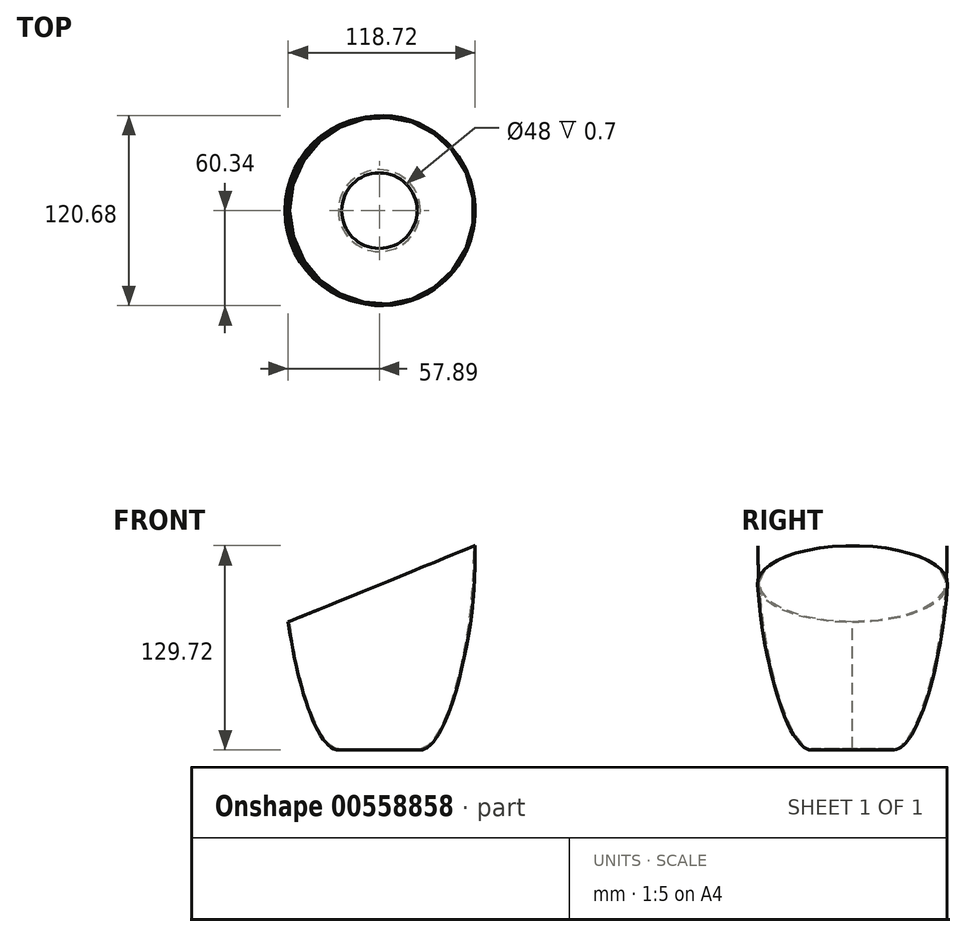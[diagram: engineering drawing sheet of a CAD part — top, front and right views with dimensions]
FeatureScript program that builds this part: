
annotation { "Feature Type Name" : "Feature", "Feature Type Description" : "" }
export const myFeature = defineFeature(function(context is Context, id is Id, definition is map)
    precondition{}
    {
        {
            var Q0;
            Q0=qCreatedBy(makeId("Front.planeOp"),FACE);
            var sketch = newSketch(context, id + "F0", { "sketchPlane" : qUnion([Q0])});
            skLineSegment(sketch, "E0", {"start": v(0, 0) * mm, "end": v(0, 79.4) * mm, "construction": true});
            skLineSegment(sketch, "E1", {"start": v(-24, 0) * mm, "end": v(-24, 0.7) * mm});
            skLineSegment(sketch, "E2", {"start": v(-26, 0) * mm, "end": v(-24, 0) * mm});
            skFitSpline(sketch, "E3", {"points": [v(-26, 0.7) * mm, v(-60, 130) * mm], "startDerivative": vector(-49.34, 0.23) * mm, "endDerivative": vector(3.08, 176.72) * mm});
            skLineSegment(sketch, "E4", {"start": v(-57.02, 130) * mm, "end": v(57.16, 130) * mm, "construction": true});
            skFitSpline(sketch, "E5.0", {"points": [v(-26, 0) * mm, v(-26.58, 0) * mm, v(-27.73, 0.16) * mm, v(-29.43, 0.83) * mm, v(-31.1, 1.89) * mm, v(-32.72, 3.3) * mm, v(-34.33, 5.07) * mm, v(-36.44, 7.86) * mm, v(-39.03, 12.13) * mm, v(-42.04, 18.4) * mm, v(-44.94, 25.72) * mm, v(-47.69, 33.96) * mm, v(-50.26, 43) * mm, v(-52.63, 52.72) * mm, v(-55.47, 66.45) * mm, v(-58.35, 84.73) * mm, v(-60.47, 107.51) * mm, v(-60.83, 122.63) * mm, v(-60.7, 130.01) * mm]});
            skLineSegment(sketch, "E6", {"start": v(-26, 0) * mm, "end": v(-26, 0) * mm});
            skLineSegment(sketch, "E7", {"start": v(-60.7, 130.01) * mm, "end": v(-60, 130) * mm});
            skLineSegment(sketch, "E8", {"start": v(-26, 0.7) * mm, "end": v(-24, 0.7) * mm});
            skSolve(sketch);
        }
        {
            var Q0;
            Q0=makeQuery(id+"F0.imprint","IMPRINT",FACE,{"disambiguationData":[TD([[makeQuery(id+"F0.imprint","IMPRINT",EDGE,{"derivedFrom":sQuery(id+"F0.wireOp",EDGE,"E1")}),1.0]])]});
            var Q1;
            Q1=sQuery(id+"F0.wireOp",EDGE,"E0");
            revolve(context, id + "F1", {"surfaceOperationType" : NewSurfaceOperationType.NEW, "entities" : qUnion([Q0]), "axis" : qUnion([Q1]), "revolveType" : RevolveType.FULL});
        }
        {
            var Q0;
            Q0=qCreatedBy(makeId("Front.planeOp"),FACE);
            var sketch = newSketch(context, id + "F2", { "sketchPlane" : qUnion([Q0])});
            skLineSegment(sketch, "E9", {"start": v(66.83, 132.22) * mm, "end": v(-75.49, 74.11) * mm});
            skLineSegment(sketch, "E10", {"start": v(-75.49, 74.11) * mm, "end": v(-75.49, 154.84) * mm});
            skLineSegment(sketch, "E11", {"start": v(-75.49, 154.84) * mm, "end": v(66.83, 154.84) * mm});
            skLineSegment(sketch, "E12", {"start": v(66.83, 154.84) * mm, "end": v(66.83, 132.22) * mm});
            skSolve(sketch);
        }
        {
            var Q0;
            Q0=makeQuery(id+"F2.imprint","IMPRINT",FACE,{"disambiguationData":[TD([[makeQuery(id+"F2.imprint","IMPRINT",EDGE,{"derivedFrom":sQuery(id+"F2.wireOp",EDGE,"E9")}),-1.0]])]});
            extrude(context, id + "F3", {"entities" : qUnion([Q0]), "operationType" : NewBodyOperationType.REMOVE, "oppositeDirection" : true, "depth" : 87.2 * mm, "offsetDistance" : 25 * mm, "hasSecondDirection" : true, "secondDirectionOppositeDirection" : false, "secondDirectionDepth" : 108.3 * mm});
        }
    });
